# Revit family: LeL Ginko 4.3
name_source: partatom
category: Lighting Fixtures
units: mm (PartAtom-declared; Revit-internal decimal feet)

## family parameters
Always vertical = No
Cut with Voids When Loaded = No
Light Source = No
OmniClass Number = 23.80.70.00
OmniClass Title = Lighting
Part Type = Normal
Room Calculation Point = No
Round Connector Dimension = Use Diameter
Shared = No
Work Plane-Based = Yes

## types (4) — shared parameters
Apparent Load = 20 VA
CCT = 3000 K
CRI = CRI80
Default Elevation = 1219 mm
Description = Outdoor Projectors
IK = IK08
IP = IP66 - IP69
Lamp = LED
Manufacturer = L&L Luce&Light srl
Model = GN43
Rated Power supply = 24 V
URL = https://www.lucelight.it
Wattage = 20 W
Weight = 2.40 kg

## per-type parameters (varying)
| type | Lumen Output | Photometry |
| L 61° | 572 lm | GN43 Light source : L 61° |
| M 34° | 625 lm | GN43 Light source : M 34° |
| S 20° | 656 lm | GN43 Light source : S 20° |
| X 32°x73° | 570 lm | GN43 Light source : X 32°x73° |

## geometry (parser evidence)
native form markers: Sweep x1
no freeform markers — native parametric forms only
